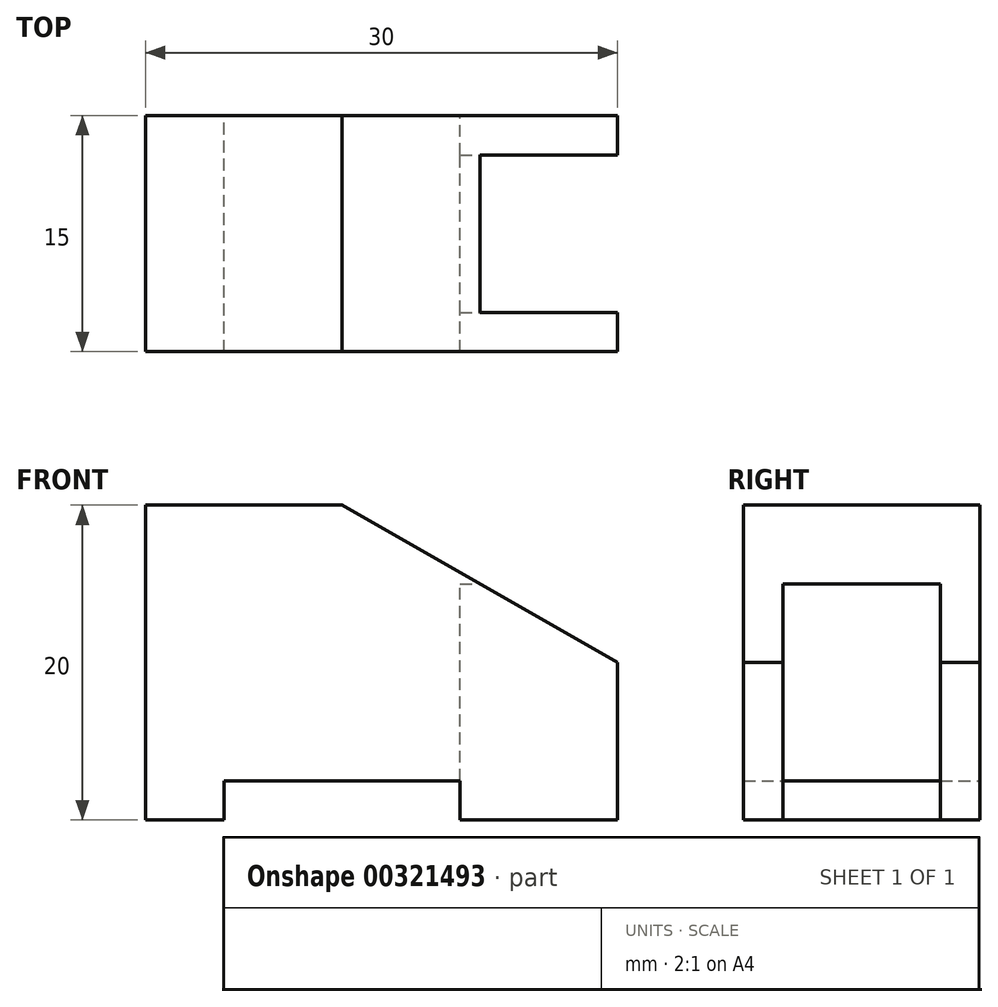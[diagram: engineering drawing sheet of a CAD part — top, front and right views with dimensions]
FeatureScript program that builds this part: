
annotation { "Feature Type Name" : "Feature", "Feature Type Description" : "" }
export const myFeature = defineFeature(function(context is Context, id is Id, definition is map)
    precondition{}
    {
        {
            var Q0;
            Q0=qCreatedBy(makeId("Front.planeOp"),FACE);
            var sketch = newSketch(context, id + "F0", { "sketchPlane" : qUnion([Q0])});
            skLineSegment(sketch, "E0", {"start": v(0, 0) * mm, "end": v(0, 20) * mm});
            skLineSegment(sketch, "E1", {"start": v(0, 20) * mm, "end": v(12.5, 20) * mm});
            skLineSegment(sketch, "E2", {"start": v(12.5, 20) * mm, "end": v(30, 10) * mm});
            skLineSegment(sketch, "E3", {"start": v(0, 0) * mm, "end": v(5, 0) * mm});
            skLineSegment(sketch, "E4", {"start": v(5, 0) * mm, "end": v(5, 2.5) * mm});
            skLineSegment(sketch, "E5", {"start": v(5, 2.5) * mm, "end": v(20, 2.5) * mm});
            skLineSegment(sketch, "E6", {"start": v(20, 2.5) * mm, "end": v(20, 0) * mm});
            skLineSegment(sketch, "E7", {"start": v(20, 0) * mm, "end": v(30, 0) * mm});
            skLineSegment(sketch, "E8", {"start": v(30, 0) * mm, "end": v(30, 10) * mm});
            skSolve(sketch);
        }
        {
            var Q0;
            Q0 = qSketchRegion(id + "F0", true);
            extrude(context, id + "F1", {"entities" : qUnion([Q0]), "depth" : 15 * mm});
        }
        {
            var Q0;
            Q0=makeQuery(id+"F1.opExtrude","SWEPT_FACE",FACE,{"disambiguationData":[OSD([sQuery(id+"F0.wireOp",EDGE,"E8")])]});
            var sketch = newSketch(context, id + "F2", { "sketchPlane" : qUnion([Q0])});
            skLineSegment(sketch, "E9.bottom", {"start": v(-12.5, 0) * mm, "end": v(-2.5, 0) * mm});
            skLineSegment(sketch, "E9.top", {"start": v(-12.5, 15) * mm, "end": v(-2.5, 15) * mm});
            skLineSegment(sketch, "E9.left", {"start": v(-12.5, 0) * mm, "end": v(-12.5, 15) * mm});
            skLineSegment(sketch, "E9.right", {"start": v(-2.5, 0) * mm, "end": v(-2.5, 15) * mm});
            skSolve(sketch);
        }
        {
            var Q0;
            Q0 = qSketchRegion(id + "F2", true);
            extrude(context, id + "F3", {"entities" : qUnion([Q0]), "operationType" : NewBodyOperationType.REMOVE, "oppositeDirection" : true, "depth" : 10 * mm});
        }
    });
